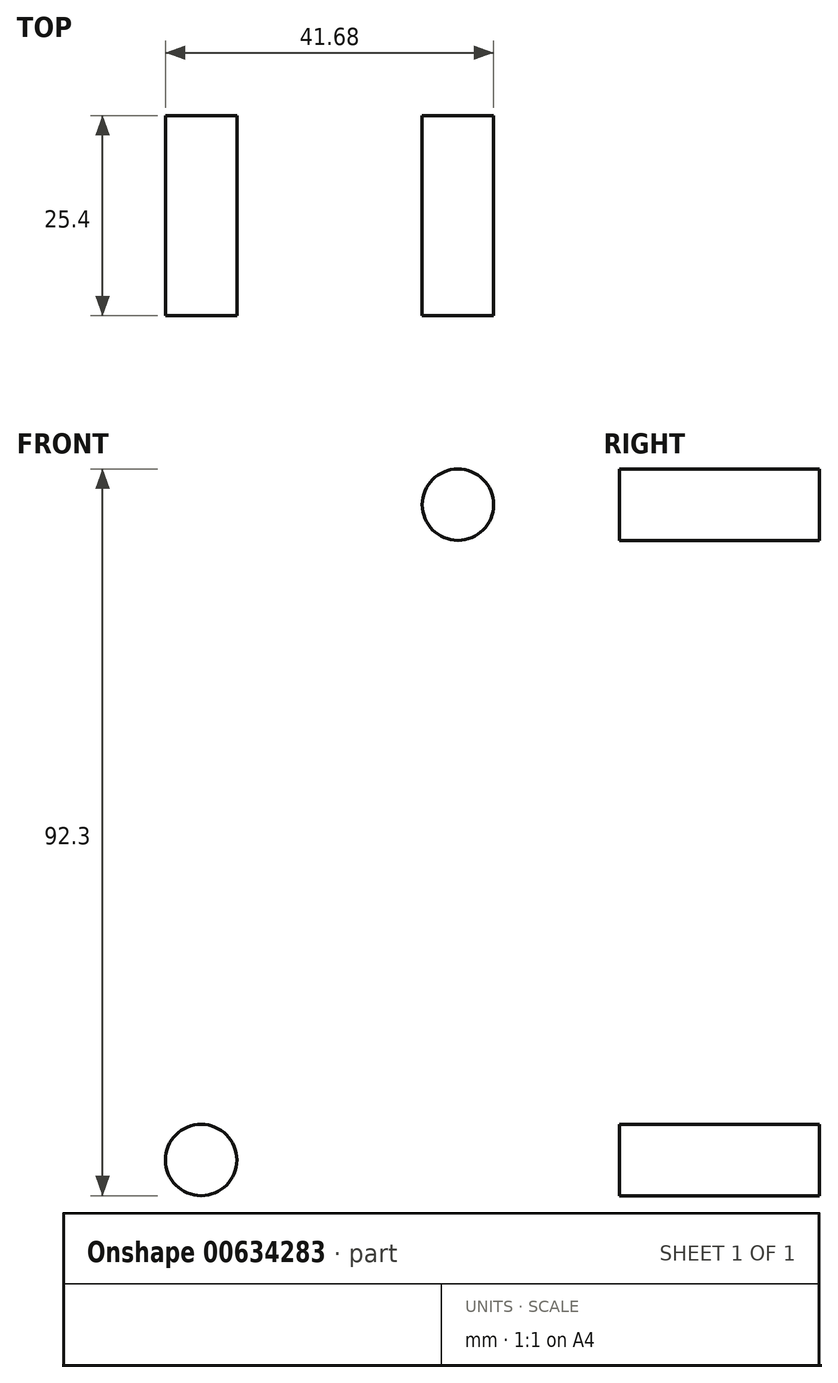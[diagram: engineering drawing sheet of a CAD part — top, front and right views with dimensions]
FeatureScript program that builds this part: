
annotation { "Feature Type Name" : "Feature", "Feature Type Description" : "" }
export const myFeature = defineFeature(function(context is Context, id is Id, definition is map)
    precondition{}
    {
        {
            var Q0;
            Q0=qCreatedBy(makeId("Front.planeOp"),FACE);
            var sketch = newSketch(context, id + "F0", { "sketchPlane" : qUnion([Q0])});
            skLineSegment(sketch, "E0.bottom", {"start": v(25.4, -50.8) * mm, "end": v(-25.4, -50.8) * mm});
            skLineSegment(sketch, "E0.top", {"start": v(25.4, 50.8) * mm, "end": v(-25.4, 50.8) * mm});
            skLineSegment(sketch, "E0.left", {"start": v(25.4, -50.8) * mm, "end": v(25.4, 50.8) * mm});
            skLineSegment(sketch, "E0.right", {"start": v(-25.4, -50.8) * mm, "end": v(-25.4, 50.8) * mm});
            skPoint(sketch, "E0.middle", {"position": v(0, 0) * mm});
            skCircle(sketch, "E1", {"center": v(0, -27.45) * mm, "radius": 7.62 * mm});
            skCircle(sketch, "E2.MirrorC", {"center": v(0, 27.45) * mm, "radius": 7.62 * mm});
            skSolve(sketch);
        }
        {
            var Q0;
            Q0=makeQuery(id+"F0.imprint","IMPRINT",FACE,{"disambiguationData":[TD([[makeQuery(id+"F0.imprint","IMPRINT",EDGE,{"derivedFrom":sQuery(id+"F0.wireOp",EDGE,"E0.bottom")}),-1.0]])]});
            extrude(context, id + "F1", {"entities" : qUnion([Q0]), "endBound" : BoundingType.SYMMETRIC, "depth" : 25.4 * mm, "offsetDistance" : 25.4 * mm});
        }
        {
            var Q0;
            Q0=makeQuery(id+"F1.opExtrude","SWEPT_EDGE",EDGE,{"disambiguationData":[OSD([sQuery(id+"F0.wireOp",EDGE,"E0.top"),sQuery(id+"F0.wireOp",EDGE,"E0.left")])]});
            var Q1;
            Q1=makeQuery(id+"F1.opExtrude","SWEPT_EDGE",EDGE,{"disambiguationData":[OSD([sQuery(id+"F0.wireOp",EDGE,"E0.top"),sQuery(id+"F0.wireOp",EDGE,"E0.right")])]});
            var Q2;
            Q2=makeQuery(id+"F1.opExtrude","SWEPT_EDGE",EDGE,{"disambiguationData":[OSD([sQuery(id+"F0.wireOp",EDGE,"E0.bottom"),sQuery(id+"F0.wireOp",EDGE,"E0.right")])]});
            var Q3;
            Q3=makeQuery(id+"F1.opExtrude","SWEPT_EDGE",EDGE,{"disambiguationData":[OSD([sQuery(id+"F0.wireOp",EDGE,"E0.bottom"),sQuery(id+"F0.wireOp",EDGE,"E0.left")])]});
            fillet(context, id + "F2", {"entities" : qUnion([Q0, Q1, Q2, Q3]), "radius" : 5.08 * mm, "tangentPropagation" : true, "allowEdgeOverflow" : false});
        }
        {
            var Q0;
            Q0=makeQuery(id+"F1.opExtrude","CAP_FACE",FACE,{"disambiguationData":[OSD([sQuery(id+"F0.wireOp",EDGE,"E0.bottom"),sQuery(id+"F0.wireOp",EDGE,"E0.top"),sQuery(id+"F0.wireOp",EDGE,"E0.left"),sQuery(id+"F0.wireOp",EDGE,"E0.right"),sQuery(id+"F0.wireOp",EDGE,"E1"),sQuery(id+"F0.wireOp",EDGE,"E2.MirrorC")])],"isStart":false});
            var sketch = newSketch(context, id + "F3", { "sketchPlane" : qUnion([Q0])});
            skCircle(sketch, "E3", {"center": v(-16.3, 41.63) * mm, "radius": 4.53 * mm});
            skCircle(sketch, "E4.MirrorC", {"center": v(16.3, 41.63) * mm, "radius": 4.53 * mm});
            skCircle(sketch, "E5.MirrorC", {"center": v(-16.3, -41.63) * mm, "radius": 4.53 * mm});
            skCircle(sketch, "E6.MirrorC", {"center": v(16.3, -41.63) * mm, "radius": 4.53 * mm});
            skSolve(sketch);
        }
        {
            var Q0;
            Q0=makeQuery(id+"F3.imprint","IMPRINT",FACE,{"disambiguationData":[TD([[makeQuery(id+"F3.imprint","IMPRINT",EDGE,{"derivedFrom":sQuery(id+"F3.wireOp",EDGE,"E3")}),1.0]])]});
            var Q1;
            Q1=makeQuery(id+"F3.imprint","IMPRINT",FACE,{"disambiguationData":[TD([[makeQuery(id+"F3.imprint","IMPRINT",EDGE,{"derivedFrom":sQuery(id+"F3.wireOp",EDGE,"E4.MirrorC")}),-1.0]])]});
            var Q2;
            Q2=makeQuery(id+"F3.imprint","IMPRINT",FACE,{"disambiguationData":[TD([[makeQuery(id+"F3.imprint","IMPRINT",EDGE,{"derivedFrom":sQuery(id+"F3.wireOp",EDGE,"E5.MirrorC")}),-1.0]])]});
            var Q3;
            Q3=makeQuery(id+"F3.imprint","IMPRINT",FACE,{"disambiguationData":[TD([[makeQuery(id+"F3.imprint","IMPRINT",EDGE,{"derivedFrom":sQuery(id+"F3.wireOp",EDGE,"E6.MirrorC")}),1.0]])]});
            var Q4;
            Q4=makeQuery(id+"F1.opExtrude","CAP_FACE",FACE,{"disambiguationData":[OSD([sQuery(id+"F0.wireOp",EDGE,"E0.bottom"),sQuery(id+"F0.wireOp",EDGE,"E0.top"),sQuery(id+"F0.wireOp",EDGE,"E0.left"),sQuery(id+"F0.wireOp",EDGE,"E0.right"),sQuery(id+"F0.wireOp",EDGE,"E1"),sQuery(id+"F0.wireOp",EDGE,"E2.MirrorC")])],"isStart":true});
            extrude(context, id + "F4", {"entities" : qUnion([Q0, Q1, Q2, Q3]), "operationType" : NewBodyOperationType.REMOVE, "endBound" : BoundingType.UP_TO_SURFACE, "oppositeDirection" : true, "depth" : 25.4 * mm, "endBoundEntityFace" : qUnion([Q4]), "offsetDistance" : 25.4 * mm});
        }
    });
